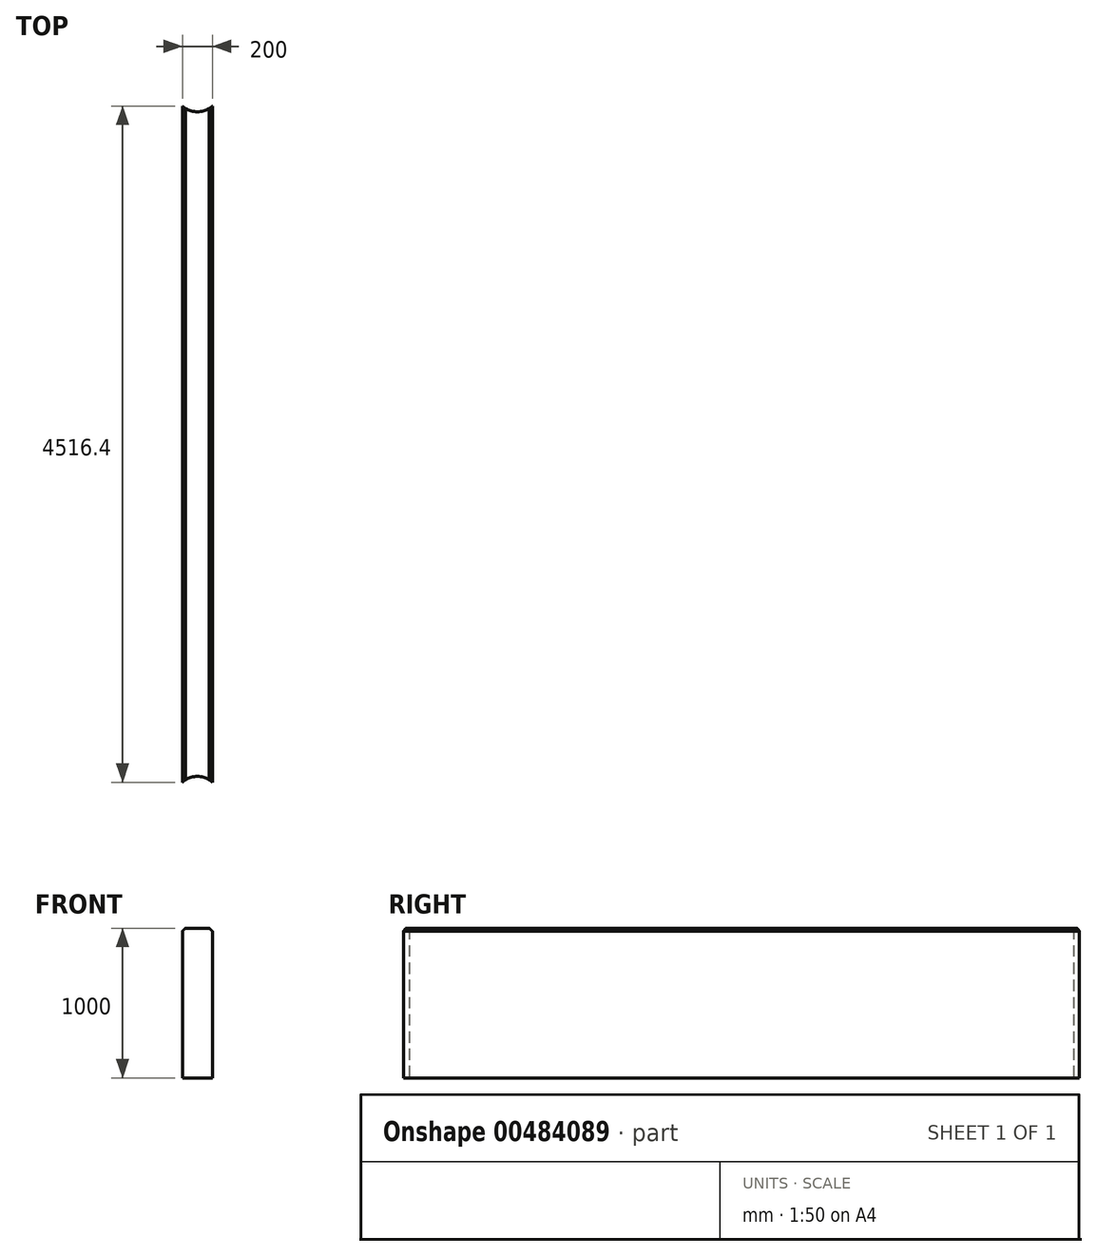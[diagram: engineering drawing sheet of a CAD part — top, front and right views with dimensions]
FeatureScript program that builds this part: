
annotation { "Feature Type Name" : "Feature", "Feature Type Description" : "" }
export const myFeature = defineFeature(function(context is Context, id is Id, definition is map)
    precondition{}
    {
        {
            var Q0;
            Q0=qCreatedBy(makeId("Top.planeOp"),FACE);
            var sketch = newSketch(context, id + "F0", { "sketchPlane" : qUnion([Q0])});
            skArc(sketch, "E0", {"start": v(100, 111.8) * mm, "mid": v(0, 151.04) * mm, "end": v(-100, 111.8) * mm});
            skArc(sketch, "E1", {"start": v(-100, 4628.2) * mm, "mid": v(0, 4590.52) * mm, "end": v(100, 4628.2) * mm});
            skLineSegment(sketch, "E2", {"start": v(-100, 111.8) * mm, "end": v(-100, 4628.2) * mm});
            skLineSegment(sketch, "E3", {"start": v(100, 111.8) * mm, "end": v(100, 4628.2) * mm});
            skSolve(sketch);
        }
        {
            var Q0;
            Q0 = qSketchRegion(id + "F0", true);
            extrude(context, id + "F1", {"entities" : qUnion([Q0]), "depth" : 1000 * mm});
        }
        {
            var Q0;
            Q0=makeQuery(id+"F1.opExtrude","CAP_EDGE",EDGE,{"disambiguationData":[OSD([sQuery(id+"F0.wireOp",EDGE,"E3")])],"isStart":false});
            var Q1;
            Q1=makeQuery(id+"F1.opExtrude","CAP_EDGE",EDGE,{"disambiguationData":[OSD([sQuery(id+"F0.wireOp",EDGE,"E2")])],"isStart":false});
            chamfer(context, id + "F2", {"entities" : qUnion([Q0, Q1]), "width" : 20 * mm, "tangentPropagation" : true});
        }
    });
